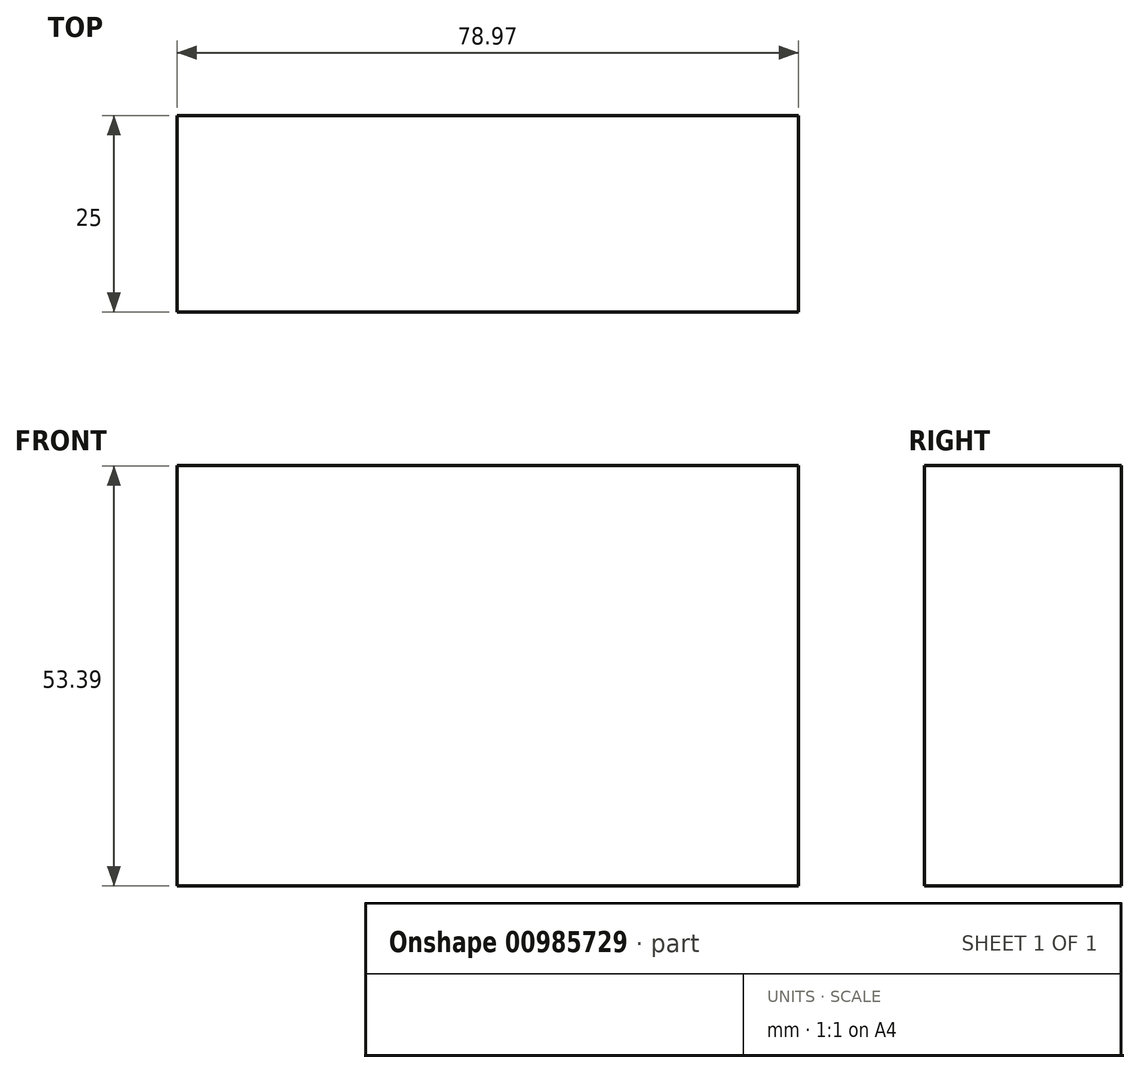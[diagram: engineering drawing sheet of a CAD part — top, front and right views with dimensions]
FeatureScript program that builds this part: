
annotation { "Feature Type Name" : "Feature", "Feature Type Description" : "" }
export const myFeature = defineFeature(function(context is Context, id is Id, definition is map)
    precondition{}
    {
        {
            var Q0;
            Q0=qCreatedBy(makeId("Front.planeOp"),FACE);
            var sketch = newSketch(context, id + "F0", { "sketchPlane" : qUnion([Q0])});
            skLineSegment(sketch, "E0.bottom", {"start": v(13.8, 20.75) * mm, "end": v(92.77, 20.75) * mm});
            skLineSegment(sketch, "E0.top", {"start": v(13.8, -32.64) * mm, "end": v(92.77, -32.64) * mm});
            skLineSegment(sketch, "E0.left", {"start": v(13.8, 20.75) * mm, "end": v(13.8, -32.64) * mm});
            skLineSegment(sketch, "E0.right", {"start": v(92.77, 20.75) * mm, "end": v(92.77, -32.64) * mm});
            skSolve(sketch);
        }
        {
            var Q0;
            Q0 = qSketchRegion(id + "F0", true);
            extrude(context, id + "F1", {"entities" : qUnion([Q0]), "depth" : 25 * mm, "offsetDistance" : 25 * mm});
        }
    });
